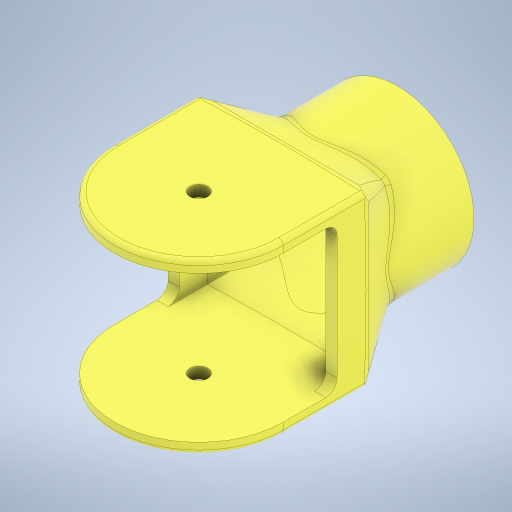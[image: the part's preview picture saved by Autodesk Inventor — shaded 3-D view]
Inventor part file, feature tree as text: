
AUTODESK INVENTOR PART (.ipt)
format: ipt  version: 2024 (Build 280153000, 153)  size: 608,256 bytes
history: native  units: mm
features: extrude x6, fillet x3, plane x2, sketch x2, loft x1, shell x1
ambient origin geometry x8: Origin, YZ Plane, XZ Plane, XY Plane, X Axis, Y Axis, Z Axis, Center Point
bodies: Body1 (feature_tree)
feature tree (15):
  plane  "Work Plane3"
  loft  "Loft1"
  extrude  "Extrusion3"  Depth=5.0mm
  shell  "Shell1"  Thickness=0.0mm
  plane  "Work Plane5"
  extrude  "Extrusion4"  TaperAngle=0.0deg  [1 undecoded]
  extrude  "Extrusion5"  Depth=5.0mm TaperAngle=0.0deg
  extrude  "Extrusion6"  Depth=5.0mm
  extrude  "Extrusion7"  Depth=5.0mm
  fillet  "Fillet1"  Radius=68.021mm
  fillet  "Fillet2"  Radius=75.0mm
  extrude  "Extrusion8"  Depth=5.0mm TaperAngle=0.0deg
  fillet  "Fillet4"  [1 undecoded]
  sketch  "Sketch17"  dims[d20=60.325mm d21=25.4mm]
  sketch  "Sketch18"  dims[d22=75.0mm d23=75.0mm d27=0.0mm d28=90.0deg d29=0.0mm d30=90.0deg d31=75.0mm d32=0.0mm d33=5.0mm d34=25.4mm d35=68.021mm d36=75.0mm d37=0.0mm d38=75.0mm d39=0.0mm d40=0.0mm d41=0.0mm d42=0.0mm d43=0.0mm d44=5.0mm d45=2.0mm d47=8.0mm d48=10.0mm d49=0.0mm d50=5.0mm]
note: 2 required parameter values undecoded (feature->parameter linkage not recoverable at this tier; creation-order binding heuristic only, values carry confidence <= 0.55)
